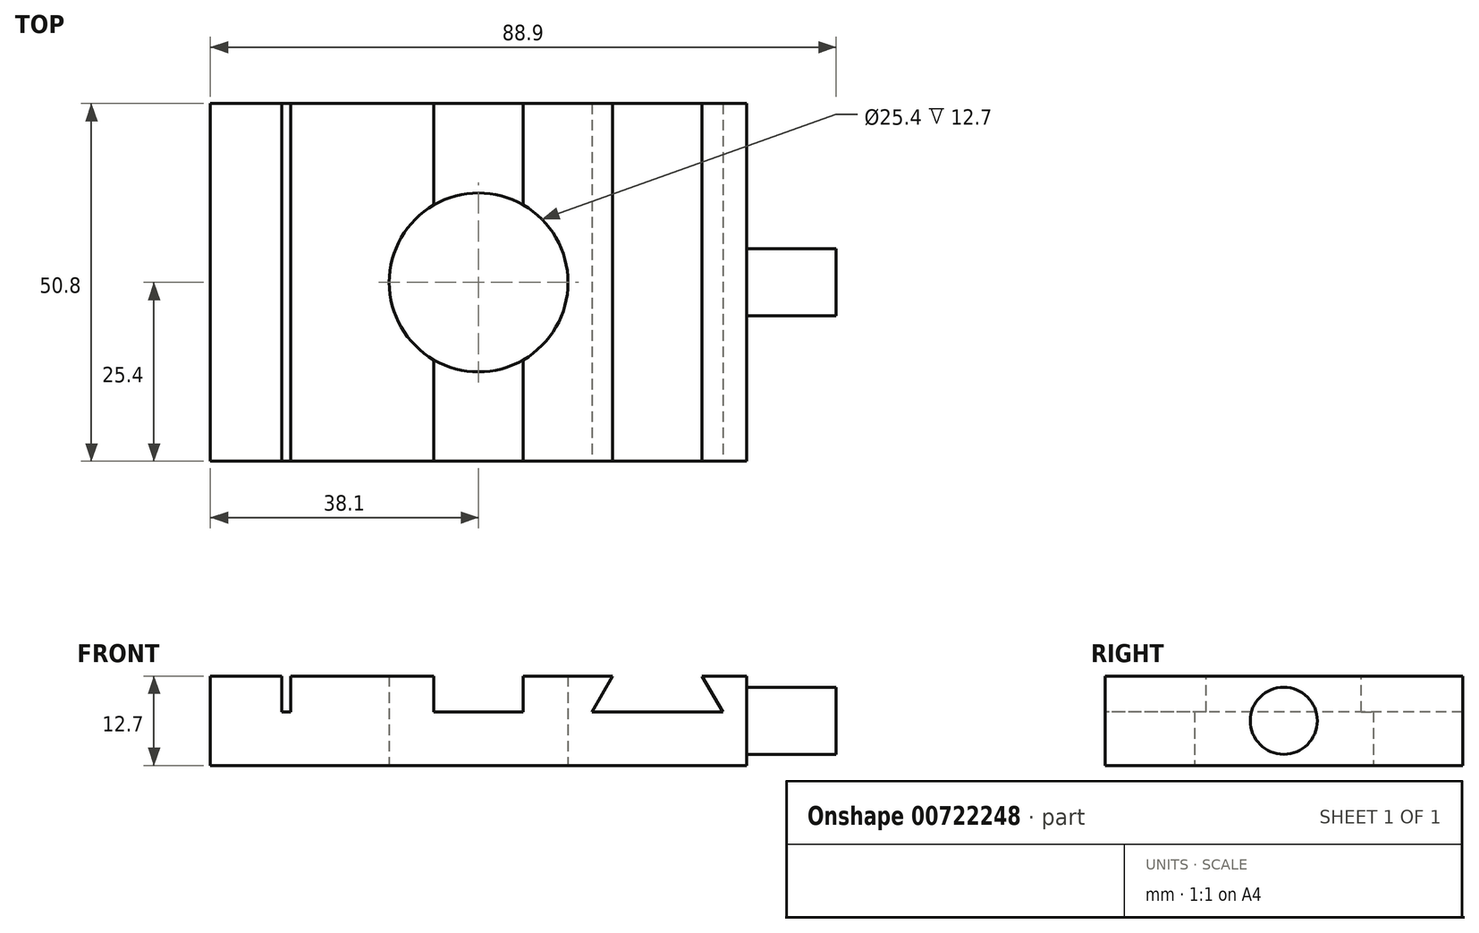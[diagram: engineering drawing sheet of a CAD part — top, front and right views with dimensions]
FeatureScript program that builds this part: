
annotation { "Feature Type Name" : "Feature", "Feature Type Description" : "" }
export const myFeature = defineFeature(function(context is Context, id is Id, definition is map)
    precondition{}
    {
        {
            var Q0;
            Q0=qCreatedBy(makeId("Top.planeOp"),FACE);
            var sketch = newSketch(context, id + "F0", { "sketchPlane" : qUnion([Q0])});
            skLineSegment(sketch, "E0.bottom", {"start": v(38.1, -25.4) * mm, "end": v(-38.1, -25.4) * mm});
            skLineSegment(sketch, "E0.top", {"start": v(38.1, 25.4) * mm, "end": v(-38.1, 25.4) * mm});
            skLineSegment(sketch, "E0.left", {"start": v(38.1, -25.4) * mm, "end": v(38.1, 25.4) * mm});
            skLineSegment(sketch, "E0.right", {"start": v(-38.1, -25.4) * mm, "end": v(-38.1, 25.4) * mm});
            skPoint(sketch, "E0.middle", {"position": v(0, 0) * mm});
            skCircle(sketch, "E1", {"center": v(0, 0) * mm, "radius": 12.7 * mm});
            skSolve(sketch);
        }
        {
            var Q0;
            Q0=makeQuery(id+"F0.imprint","IMPRINT",FACE,{"disambiguationData":[TD([[makeQuery(id+"F0.imprint","IMPRINT",EDGE,{"derivedFrom":sQuery(id+"F0.wireOp",EDGE,"E0.bottom")}),-1.0]])]});
            extrude(context, id + "F1", {"entities" : qUnion([Q0]), "depth" : 12.7 * mm, "offsetDistance" : 25.4 * mm});
        }
        {
            var Q0;
            Q0=makeQuery(id+"F1.opExtrude","CAP_FACE",FACE,{"disambiguationData":[OSD([sQuery(id+"F0.wireOp",EDGE,"E0.bottom"),sQuery(id+"F0.wireOp",EDGE,"E0.top"),sQuery(id+"F0.wireOp",EDGE,"E0.left"),sQuery(id+"F0.wireOp",EDGE,"E0.right"),sQuery(id+"F0.wireOp",EDGE,"E1")])],"isStart":false});
            var sketch = newSketch(context, id + "F2", { "sketchPlane" : qUnion([Q0])});
            skLineSegment(sketch, "E2.bottom", {"start": v(-27.94, 25.4) * mm, "end": v(-26.67, 25.4) * mm});
            skLineSegment(sketch, "E2.top", {"start": v(-27.94, -25.4) * mm, "end": v(-26.67, -25.4) * mm});
            skLineSegment(sketch, "E2.left", {"start": v(-27.94, 25.4) * mm, "end": v(-27.94, -25.4) * mm});
            skLineSegment(sketch, "E2.right", {"start": v(-26.67, 25.4) * mm, "end": v(-26.67, -25.4) * mm});
            skLineSegment(sketch, "E3", {"start": v(-6.35, 25.4) * mm, "end": v(-6.35, -25.4) * mm});
            skLineSegment(sketch, "E4", {"start": v(6.35, 25.4) * mm, "end": v(6.35, -25.4) * mm});
            skLineSegment(sketch, "E5", {"start": v(-6.35, 25.4) * mm, "end": v(6.35, 25.4) * mm, "construction": true});
            skLineSegment(sketch, "E6", {"start": v(-6.35, -25.4) * mm, "end": v(6.35, -25.4) * mm, "construction": true});
            skLineSegment(sketch, "E7", {"start": v(0, 25.4) * mm, "end": v(0, -25.4) * mm, "construction": true});
            skSolve(sketch);
        }
        {
            var Q0;
            Q0=makeQuery(id+"F2.imprint","IMPRINT",FACE,{"disambiguationData":[TD([[makeQuery(id+"F2.imprint","IMPRINT",EDGE,{"derivedFrom":sQuery(id+"F2.wireOp",EDGE,"E2.bottom")}),1.0]])]});
            var Q1;
            {var subQ0=sQuery(id+"F2.wireOp",EDGE,"E3");var subQ1=makeQuery(id+"F1.opExtrude","CAP_EDGE",EDGE,{"disambiguationData":[OSD([sQuery(id+"F0.wireOp",EDGE,"E0.bottom")])],"isStart":false});var subQ2=makeQuery(id+"F2.imprint","INTERSECT",VERTEX,{"derivedFrom":[subQ1,subQ0]});Q1=makeQuery(id+"F2.imprint","IMPRINT",FACE,{"disambiguationData":[TD([[makeQuery(id+"F2.imprint","IMPRINT",EDGE,{"disambiguationData":[TD([[subQ2,1.0]])],"derivedFrom":subQ0}),1.0]])]});}
            var Q2;
            {var subQ0=sQuery(id+"F2.wireOp",EDGE,"E3");var subQ1=makeQuery(id+"F1.opExtrude","CAP_EDGE",EDGE,{"disambiguationData":[OSD([sQuery(id+"F0.wireOp",EDGE,"E0.top")])],"isStart":false});var subQ2=makeQuery(id+"F2.imprint","INTERSECT",VERTEX,{"derivedFrom":[subQ1,subQ0]});Q2=makeQuery(id+"F2.imprint","IMPRINT",FACE,{"disambiguationData":[TD([[makeQuery(id+"F2.imprint","IMPRINT",EDGE,{"disambiguationData":[TD([[subQ2,-1.0]])],"derivedFrom":subQ0}),1.0]])]});}
            extrude(context, id + "F3", {"entities" : qUnion([Q0, Q1, Q2]), "operationType" : NewBodyOperationType.REMOVE, "oppositeDirection" : true, "depth" : 5.08 * mm, "offsetDistance" : 25.4 * mm});
        }
        {
            var Q0;
            Q0=makeQuery(id+"F1.opExtrude","SWEPT_FACE",FACE,{"disambiguationData":[OSD([sQuery(id+"F0.wireOp",EDGE,"E0.bottom")])]});
            var sketch = newSketch(context, id + "F4", { "sketchPlane" : qUnion([Q0])});
            skLineSegment(sketch, "E8", {"start": v(19.05, 12.7) * mm, "end": v(16.12, 7.62) * mm});
            skLineSegment(sketch, "E9", {"start": v(16.12, 7.62) * mm, "end": v(34.68, 7.62) * mm});
            skLineSegment(sketch, "E10", {"start": v(34.68, 7.62) * mm, "end": v(31.75, 12.7) * mm});
            skLineSegment(sketch, "E11", {"start": v(31.75, 12.7) * mm, "end": v(19.05, 12.7) * mm});
            skLineSegment(sketch, "E12", {"start": v(25.4, 7.62) * mm, "end": v(25.4, 12.7) * mm, "construction": true});
            skSolve(sketch);
        }
        {
            var Q0;
            Q0=makeQuery(id+"F4.imprint","IMPRINT",FACE,{"disambiguationData":[TD([[makeQuery(id+"F4.imprint","IMPRINT",EDGE,{"derivedFrom":sQuery(id+"F4.wireOp",EDGE,"E8")}),1.0]])]});
            extrude(context, id + "F5", {"entities" : qUnion([Q0]), "operationType" : NewBodyOperationType.REMOVE, "endBound" : BoundingType.THROUGH_ALL, "oppositeDirection" : true, "depth" : 25.4 * mm, "offsetDistance" : 25.4 * mm});
        }
        {
            var Q0;
            Q0=makeQuery(id+"F1.opExtrude","SWEPT_FACE",FACE,{"disambiguationData":[OSD([sQuery(id+"F0.wireOp",EDGE,"E0.left")])]});
            var sketch = newSketch(context, id + "F6", { "sketchPlane" : qUnion([Q0])});
            skCircle(sketch, "E13", {"center": v(0, 6.35) * mm, "radius": 4.76 * mm});
            skPoint(sketch, "E13.centerSnap0", {"position": v(-25.4, 6.35) * mm});
            skPoint(sketch, "E13.centerSnap1", {"position": v(0, 12.7) * mm});
            skSolve(sketch);
        }
        {
            var Q0;
            Q0=makeQuery(id+"F6.imprint","IMPRINT",FACE,{"disambiguationData":[TD([[makeQuery(id+"F6.imprint","IMPRINT",EDGE,{"derivedFrom":sQuery(id+"F6.wireOp",EDGE,"E13")}),1.0]])]});
            extrude(context, id + "F7", {"entities" : qUnion([Q0]), "operationType" : NewBodyOperationType.ADD, "depth" : 12.7 * mm, "offsetDistance" : 25.4 * mm});
        }
    });
